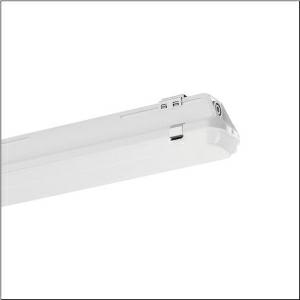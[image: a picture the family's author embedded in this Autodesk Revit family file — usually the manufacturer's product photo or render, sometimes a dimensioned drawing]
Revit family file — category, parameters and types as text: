
# Revit family: monsun_r__21_51fb10ml660k_5e6a
name_source: partatom
category: Lighting Fixtures
units: mm (PartAtom-declared; Revit-internal decimal feet)

## family parameters
Cut with Voids When Loaded = No
Host = Face
Light Source = No
Part Type = Normal
Room Calculation Point = No
Round Connector Dimension = Use Diameter
Shared = No

## types (1)
- --- (1 x LED, 5960 lm, 34.1 W, 6500K)
    Apparent Load = 34 VA
    CIE Flux Codes = 46 76 93 94 100
    Color Rendering = 80
    Color Temperature = 6500K
    Default Elevation = 1800 mm
    Description = Monsun® 21, damp-proof luminaire, chain hanger, primary optical cover: enclosure, of PMMA, light emission: direct distribution, primary light characteristic: symmetric, installation type: suspended mounting, surface-mounted, horizontal mounting, vertical mounting, LED, rated luminous flux: 5.960lm, luminous efficacy: 175lm/W, light colour: 865, colour temperature: 6500K, control gear: ON/OFF Multilumen, with terminal, 3-pole, max. 2.5mm², mains connection: 220..240V, AC, 50/60Hz, rated input power: 34W, housing, of glass-fibre reinforced plastic, uncoated, bright grey, incl. chain hanger, length: 1.299mm, width: 90mm, height: 88mm, clip for enclosure, of stainless steel (V2A), ceiling mounting element, of stainless steel (V2A), chain hanger, of stainless steel (V2A), protection rating (complete): IP66, insulation class (complete): insulation class I (protective earthing), certification: CE, ENEC, VDE, UKCA, protection symbol: D, impact resistance: IK04, permissible operating ambient temperature: -25..+35°C, standard: EN 50419, EN 60598-2-1, corresponds to IFS (International Featured Standards) requirements for safety and quality in the food industry, for indoor or canopied outdoor use, no direct snow, no direct sun, no direct rain, LABS conformity tested according to VDMA 24364:2018-05, contact your sales advisor before using the luminaires in applications with unclear chemical exposure, large temperature fluctuations or condensation-forming humidity, packaging unit: 1 piece
    Height = 88 mm
    Lamp = 1 x LED
    Lamp Light Flux = 5960 lm
    Lamp Power = 34.1 W
    Lamp count = 1
    Length = 1299 mm
    Luminous efficacy = 175 lm/W
    Manufacturer = Siteco
    ModVariant = No
    Model = 51FB10ML660K
    Mounting Place = Ceiling
    Mounting Type = Surface mounted
    Number of Poles = 1
    OnlyDefault = Yes
    Power Factor = 1
    Product Name = Monsun® 21
    Product group = damp-proof luminaire
    ProductGroupID = 300
    Protection Class = Protection class I
    Protection Degree = IP 66
    RLX_Detail_Level = 1
    RLX_Emergency_Light_Flux = 0 lm
    RLX_Emergency_Type = 0
    RLX_Emergency_Type_DB = No
    RlxData = <blob elided: 90965 chars, md5=659b1428>
    Socket = socket
    Standby Power = 0 W
    System Light Flux = 5960 lm
    System Power = 34 W
    Type Comments = factory setting: luminous flux: 100 % | (A | C | E) | 79 mA
    Type Image = l_1319656.jpg
    URL = http://relux.com
    VarID = @adj_042170
    Voltage = 0 V
    Weight = 0.00 kg
    Width = 90 mm

## geometry (parser evidence)
native form markers: Blend x4, Sweep x14
no freeform markers — native parametric forms only
